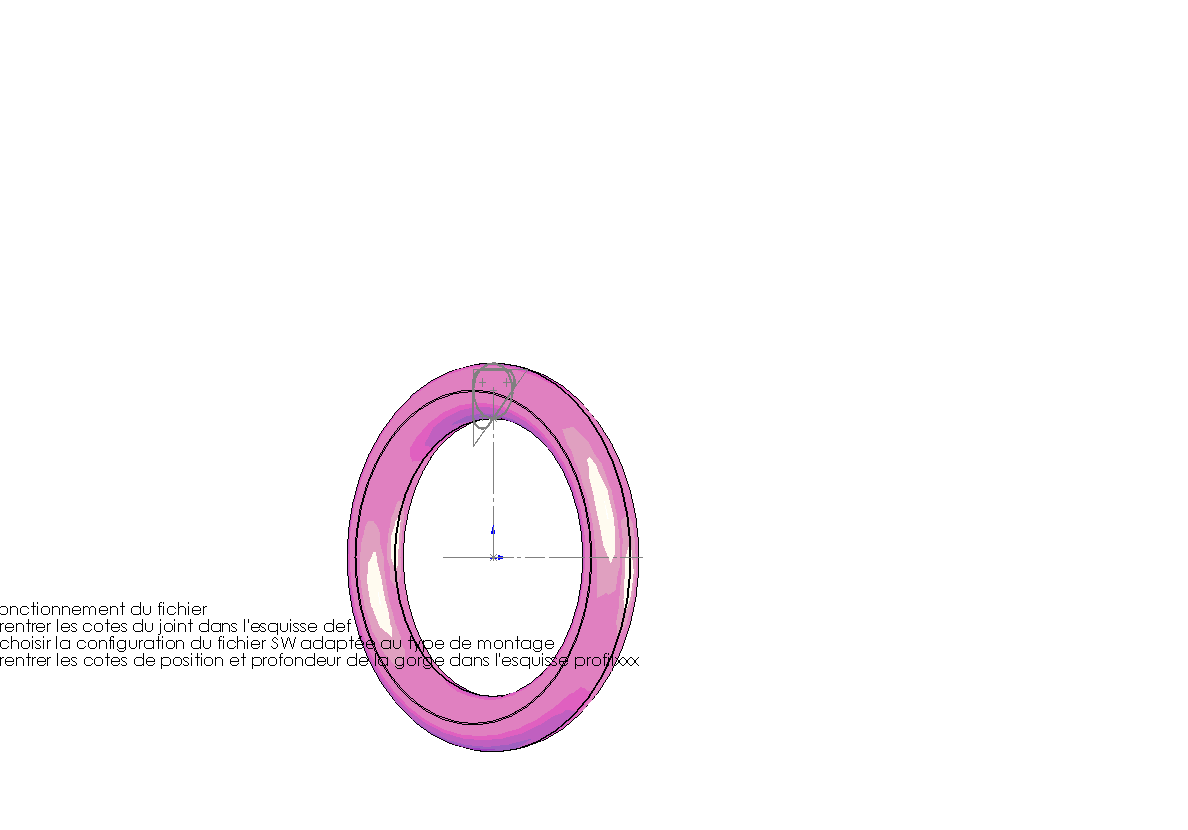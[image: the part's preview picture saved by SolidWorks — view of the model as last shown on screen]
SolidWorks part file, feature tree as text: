
SOLIDWORKS PART (.sldprt)
format: sldprt  version: not decoded by parser v0  size: 1,345,536 bytes
history: native  units: mm
features: sketch x8, revolve x6, plane x3, material x1 (+12 scaffold rows collapsed)
feature tree (30):
  scaffold x12  (default folders/planes/origin — collapsed)
  material  "Matériau <non spécifié>"
  plane  "Plan de face"
  plane  "Plan de dessus"
  plane  "Plan de droite"
  sketch  "def"  dims[c1.D1=~3.306807mm c1.D2=~4.340992mm c1.D3=~8.681984mm c2.D2=10.0mm c2.D3=4.0mm c2.D4=~20.000109mm c3.D3=0.1mm c3.D4=0.05mm c4.D3=~14.089796mm c4.D4=~8.730487mm]
  sketch  "calcul"  dims[c1.D1=~3.306807mm c1.D2=~4.340992mm c1.D3=~8.681984mm c2.D2=6.07mm c2.D3=4.0mm c2.D4=~20.000109mm c3.D3=0.1mm c3.D4=0.05mm c3.vol=~118.435253mm c3.d=1.45mm c3.a=1.5mm c3.b=~13.767146mm c3.c=~42.286226mm c4.D4=~19.154567mm c4.delta=~443.251662mm]
  sketch  "profilrad"  dims[c1.D1=0.665mm c1.D3=0.725mm c1.D2=5.0mm c2.D3=2.28mm c2.D4=~46.138391mm c3.D3=2.28mm c3.D1=~0.558547mm c3.D2=~0.33379mm c4.D1=4.0mm c4.D2=~2.029157mm c4.D4=~2.680334mm c4.D5=0.05mm c4.D6=~0.336496mm c5.D2=5.0mm c5.D4=~2.970843mm c6.D2=5.0mm c6.D4=9.0mm c6.D1=~5.43667mm c6.D6=4.0mm c7.D1=~1.705666mm c7.vol=~19.534376mm]
  sketch  "profil"  dims[c1.D1=0.665mm c1.D3=0.975mm c1.D2=5.0mm c2.D3=2.28mm c2.D4=~46.138391mm c3.D3=2.28mm c3.D1=~0.558547mm c3.D2=~0.33379mm c4.D1=4.0mm c4.D2=~2.029157mm c4.D4=~2.680334mm c4.D5=0.05mm c4.D6=~0.336496mm c5.D2=5.0mm c5.D4=~2.970843mm c6.D2=10.0mm c6.D4=9.0mm c6.D1=0.05mm c6.D6=~2.058362mm c6.vol=~19.534376mm c7.D4=2.0mm]
  revolve  "défaut"  Angle=360deg
  revolve  "radial"  Angle=360deg
  sketch  "profilai"  dims[c1.D1=0.665mm c1.D3=0.725mm c1.D2=5.0mm c2.D3=2.28mm c2.D4=~46.138391mm c3.D3=2.28mm c3.D1=~0.558547mm c3.D2=~0.33379mm c4.D1=4.0mm c4.D2=~2.029157mm c4.D4=~2.680334mm c4.D5=~34.50683mm c4.D6=~0.336496mm c5.D2=5.0mm c5.D4=~2.970843mm c6.D2=9.5mm c6.D4=9.0mm c6.D1=0.05mm c6.D6=1.5mm c6.vol=~19.534376mm c7.D4=~35.93383mm c7.D5=~2.428799mm]
  revolve  "axial dint"  Angle=360deg
  sketch  "profilae"  dims[c1.D1=0.665mm c1.D3=0.625mm c1.D2=5.0mm c2.D3=2.28mm c2.D4=~46.138391mm c3.D3=2.28mm c3.D1=~0.558547mm c3.D2=~0.33379mm c4.D1=4.0mm c4.D2=~2.029157mm c4.D4=~2.680334mm c4.D5=~48.435314mm c4.D6=~0.336496mm c5.D2=5.0mm c5.D4=~2.970843mm c6.D2=5.5mm c6.D4=9.0mm c6.D1=0.05mm c6.D6=1.7mm c6.vol=~19.534376mm c7.D2=13.5mm c7.D4=~50.455314mm c7.D5=~3.055497mm]
  revolve  "axial dext"  Angle=360deg
  sketch  "profilchi"  dims[c1.D1=0.665mm c1.D3=0.85mm c2.D1=~0.947199mm c2.D3=~0.190364mm c2.D5=~0.801402mm c3.D3=~0.390555mm c3.D2=5.0mm c4.D3=2.28mm c4.D4=~46.138391mm c5.D3=2.28mm c5.D1=~0.558547mm c5.D2=~0.33379mm c6.D1=4.0mm c6.D2=~2.029157mm c6.D4=~2.680334mm c6.D5=0.05mm c6.D6=~0.336496mm c7.D2=5.0mm c7.D4=~2.970843mm c8.D2=6.0mm c8.D4=9.5mm c8.D1=~0.108362mm c8.D6=~1.808362mm c8.vol=~19.534376mm c8.D7=~4.311519mm c9.D7=~56.448093deg c9.D4=45.0deg c9.D8=~5.516098mm c9.D2=2.64mm c9.D9=~11.197838mm c9.D1=10.5mm c9.D5=~0.542834mm c10.D4=2.41mm c11.D4=45.0deg c11.D5=~2.489094mm]
  revolve  "chanfrein dint"  Angle=360deg
  sketch  "profilche"  dims[c1.D1=0.665mm c1.D3=0.85mm c2.D1=~0.947199mm c2.D3=~0.44174mm c2.D5=~0.801402mm c2.D2=5.0mm c3.D3=2.28mm c3.D4=~46.138391mm c4.D3=2.28mm c4.D1=~0.558547mm c4.D2=~0.33379mm c5.D1=4.0mm c5.D2=~2.029157mm c5.D4=~2.680334mm c5.D5=0.05mm c5.D6=~0.336496mm c6.D2=5.0mm c6.D4=~2.970843mm c7.D2=6.0mm c7.D4=9.5mm c7.D1=~0.108362mm c7.D6=~1.808362mm c7.vol=~19.534376mm c7.D7=~4.311519mm c8.D7=~56.448093deg c8.D4=45.0deg c8.D8=~5.516098mm c8.D2=2.74mm c8.D9=~11.197838mm c8.D1=13.5mm c8.D5=~0.542834mm]
  revolve  "chanfrein dext"  Angle=360deg
decode coverage: 14 of 14 modeling features carry decoded parameters
note: ~ marks probable driven/reference dimensions
note: suppression state not decoded; provenance and decode notes live in map.json
